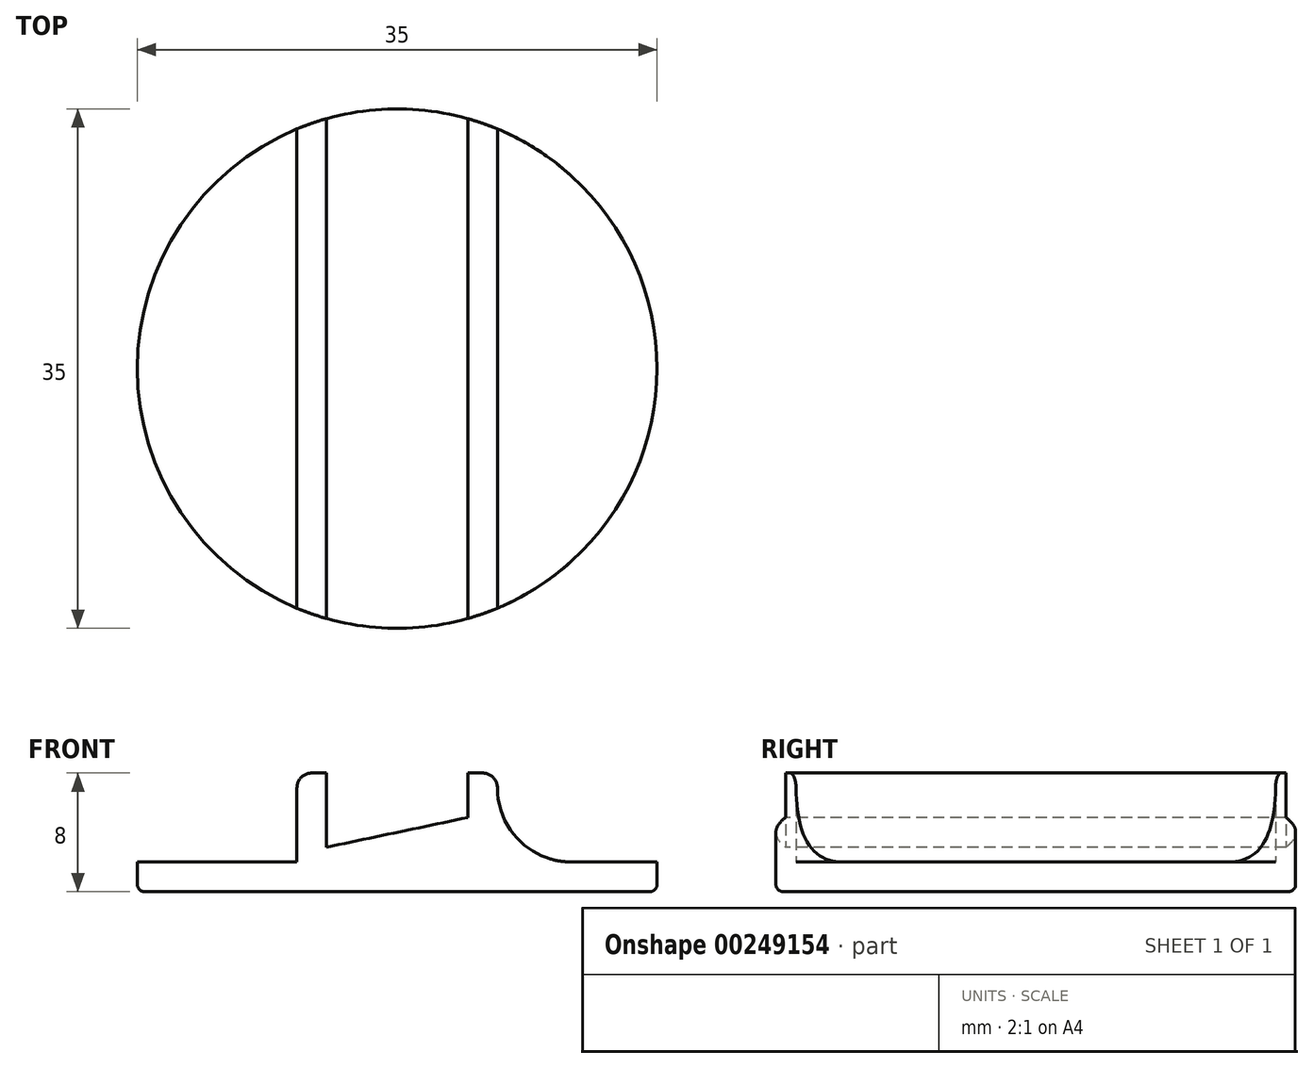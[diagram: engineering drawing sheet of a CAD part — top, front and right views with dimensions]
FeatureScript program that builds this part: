
annotation { "Feature Type Name" : "Feature", "Feature Type Description" : "" }
export const myFeature = defineFeature(function(context is Context, id is Id, definition is map)
    precondition{}
    {
        {
            var Q0;
            Q0=qCreatedBy(makeId("Top.planeOp"),FACE);
            var sketch = newSketch(context, id + "F0", { "sketchPlane" : qUnion([Q0])});
            skCircle(sketch, "E0", {"center": v(0, 0) * mm, "radius": 17.5 * mm});
            skSolve(sketch);
        }
        {
            var Q0;
            Q0=makeQuery(id+"F0.imprint","IMPRINT",FACE,{"disambiguationData":[TD([[makeQuery(id+"F0.imprint","IMPRINT",EDGE,{"derivedFrom":sQuery(id+"F0.wireOp",EDGE,"E0")}),1.0]])]});
            extrude(context, id + "F1", {"entities" : qUnion([Q0]), "depth" : 2 * mm});
        }
        {
            var Q0;
            Q0=qCreatedBy(makeId("Front.planeOp"),FACE);
            var sketch = newSketch(context, id + "F2", { "sketchPlane" : qUnion([Q0])});
            skLineSegment(sketch, "E1.0", {"start": v(-17.5, 2) * mm, "end": v(17.5, 2) * mm});
            skLineSegment(sketch, "E2", {"start": v(-6.75, 8) * mm, "end": v(-6.75, 2) * mm});
            skLineSegment(sketch, "E3", {"start": v(6.75, 8) * mm, "end": v(6.75, 2) * mm});
            skLineSegment(sketch, "E4", {"start": v(-6.75, 8) * mm, "end": v(-4.75, 8) * mm});
            skLineSegment(sketch, "E5", {"start": v(-4.75, 8) * mm, "end": v(-4.75, 3) * mm});
            skLineSegment(sketch, "E6", {"start": v(-4.75, 3) * mm, "end": v(4.75, 5) * mm});
            skLineSegment(sketch, "E7", {"start": v(4.75, 5) * mm, "end": v(4.75, 8) * mm});
            skLineSegment(sketch, "E8", {"start": v(4.75, 8) * mm, "end": v(6.75, 8) * mm});
            skSolve(sketch);
        }
        {
            var Q0;
            {var subQ1=sQuery(id+"F2.wireOp",EDGE,"E2");Q0=makeQuery(id+"F2.imprint","IMPRINT",FACE,{"disambiguationData":[TD([[makeQuery(id+"F2.imprint","IMPRINT",EDGE,{"derivedFrom":subQ1}),1.0]])]});}
            extrude(context, id + "F3", {"entities" : qUnion([Q0]), "operationType" : NewBodyOperationType.ADD, "endBound" : BoundingType.SYMMETRIC, "oppositeDirection" : true, "depth" : 40 * mm});
        }
        {
            var Q0;
            {var subQ0=sQuery(id+"F2.wireOp",EDGE,"E2");var subQ1=sQuery(id+"F2.wireOp",EDGE,"E3");var subQ2=sQuery(id+"F2.wireOp",EDGE,"E1.0");Q0=makeQuery(id+"F3.boolean.opBoolean","SPLIT",FACE,{"disambiguationData":[TD([makeQuery(id+"F3.opExtrude","CAP_FACE",FACE,{"disambiguationData":[OSD([subQ2,subQ0,subQ1,sQuery(id+"F2.wireOp",EDGE,"E4"),sQuery(id+"F2.wireOp",EDGE,"E5"),sQuery(id+"F2.wireOp",EDGE,"E6"),sQuery(id+"F2.wireOp",EDGE,"E7"),sQuery(id+"F2.wireOp",EDGE,"E8")])],"isStart":true})])],"derivedFrom":makeQuery(id+"F3.opExtrude","SWEPT_FACE",FACE,{"disambiguationData":[OSD([subQ2])]})});}
            extrude(context, id + "F4", {"entities" : qUnion([Q0]), "operationType" : NewBodyOperationType.REMOVE, "endBound" : BoundingType.UP_TO_NEXT, "oppositeDirection" : true, "depth" : 25 * mm});
        }
        {
            var Q0;
            {var subQ0=sQuery(id+"F2.wireOp",EDGE,"E2");var subQ2=sQuery(id+"F2.wireOp",EDGE,"E3");var subQ3=sQuery(id+"F2.wireOp",EDGE,"E1.0");Q0=makeQuery(id+"F3.boolean.opBoolean","SPLIT",FACE,{"disambiguationData":[TD([makeQuery(id+"F3.opExtrude","CAP_FACE",FACE,{"disambiguationData":[OSD([subQ3,subQ0,subQ2,sQuery(id+"F2.wireOp",EDGE,"E4"),sQuery(id+"F2.wireOp",EDGE,"E5"),sQuery(id+"F2.wireOp",EDGE,"E6"),sQuery(id+"F2.wireOp",EDGE,"E7"),sQuery(id+"F2.wireOp",EDGE,"E8")])],"isStart":false})])],"derivedFrom":makeQuery(id+"F3.opExtrude","SWEPT_FACE",FACE,{"disambiguationData":[OSD([subQ3])]})});}
            extrude(context, id + "F5", {"entities" : qUnion([Q0]), "operationType" : NewBodyOperationType.REMOVE, "endBound" : BoundingType.UP_TO_NEXT, "oppositeDirection" : true, "depth" : 25 * mm});
        }
        {
            var Q0;
            {var subQ0=sQuery(id+"F2.wireOp",EDGE,"E2");Q0=makeQuery(id+"F3.boolean.opBoolean","SPLIT",EDGE,{"disambiguationData":[topologyDisambiguationEdgeConnected([makeQuery(id+"F1.opExtrude","CAP_FACE",FACE,{"disambiguationData":[OSD([sQuery(id+"F0.wireOp",EDGE,"E0")])],"isStart":false}),makeQuery(id+"F3.opExtrude","SWEPT_FACE",FACE,{"disambiguationData":[OSD([subQ0])]})])],"derivedFrom":makeQuery(id+"F3.opExtrude","SWEPT_EDGE",EDGE,{"disambiguationData":[OSD([sQuery(id+"F2.wireOp",EDGE,"E1.0"),subQ0])]})});}
            var Q1;
            {var subQ0=sQuery(id+"F2.wireOp",EDGE,"E3");Q1=makeQuery(id+"F3.boolean.opBoolean","SPLIT",EDGE,{"disambiguationData":[topologyDisambiguationEdgeConnected([makeQuery(id+"F1.opExtrude","CAP_FACE",FACE,{"disambiguationData":[OSD([sQuery(id+"F0.wireOp",EDGE,"E0")])],"isStart":false}),makeQuery(id+"F3.opExtrude","SWEPT_FACE",FACE,{"disambiguationData":[OSD([subQ0])]})])],"derivedFrom":makeQuery(id+"F3.opExtrude","SWEPT_EDGE",EDGE,{"disambiguationData":[OSD([sQuery(id+"F2.wireOp",EDGE,"E1.0"),subQ0])]})});}
            fillet(context, id + "F6", {"entities" : qUnion([Q0, Q1]), "radius" : 5 * mm, "tangentPropagation" : true, "allowEdgeOverflow" : false});
        }
        {
            var Q0;
            Q0=makeQuery(id+"F3.opExtrude","SWEPT_EDGE",EDGE,{"disambiguationData":[OSD([sQuery(id+"F2.wireOp",EDGE,"E2"),sQuery(id+"F2.wireOp",EDGE,"E4")])]});
            var Q1;
            Q1=makeQuery(id+"F3.opExtrude","SWEPT_EDGE",EDGE,{"disambiguationData":[OSD([sQuery(id+"F2.wireOp",EDGE,"E3"),sQuery(id+"F2.wireOp",EDGE,"E8")])]});
            fillet(context, id + "F7", {"entities" : qUnion([Q0, Q1]), "radius" : 1 * mm, "tangentPropagation" : true, "allowEdgeOverflow" : false});
        }
        {
            var Q0;
            Q0=makeQuery(id+"F1.opExtrude","CAP_EDGE",EDGE,{"disambiguationData":[OSD([sQuery(id+"F0.wireOp",EDGE,"E0")])],"isStart":true});
            fillet(context, id + "F8", {"entities" : qUnion([Q0]), "radius" : .5 * mm, "tangentPropagation" : true, "allowEdgeOverflow" : false});
        }
    });
